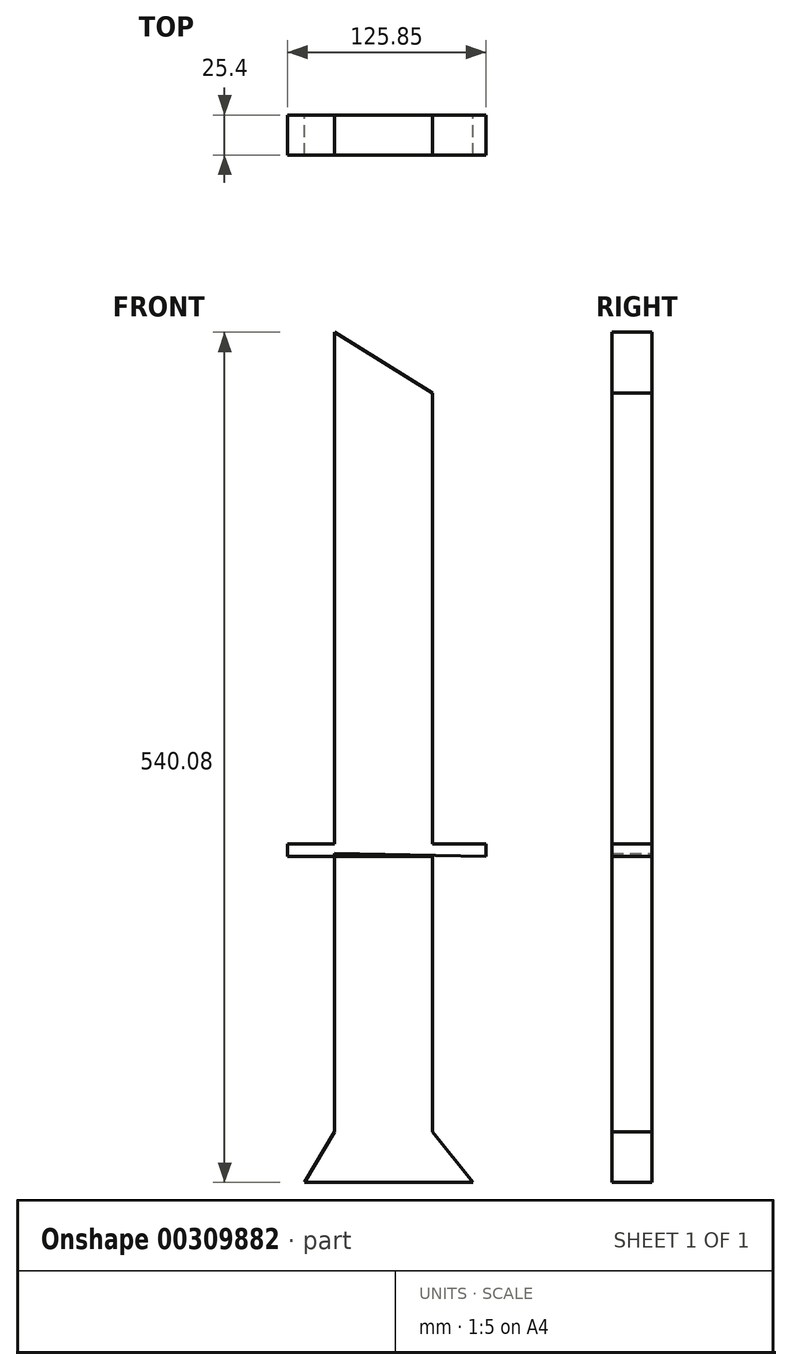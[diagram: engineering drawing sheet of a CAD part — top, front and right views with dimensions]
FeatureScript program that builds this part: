
annotation { "Feature Type Name" : "Feature", "Feature Type Description" : "" }
export const myFeature = defineFeature(function(context is Context, id is Id, definition is map)
    precondition{}
    {
        {
            var Q0;
            Q0=qCreatedBy(makeId("Front.planeOp"),FACE);
            var sketch = newSketch(context, id + "F0", { "sketchPlane" : qUnion([Q0])});
            skLineSegment(sketch, "E0.bottom", {"start": v(-29.82, 5.84) * mm, "end": v(78.28, 5.84) * mm});
            skLineSegment(sketch, "E0.top", {"start": v(-29.82, -2.03) * mm, "end": v(78.28, -2.03) * mm});
            skLineSegment(sketch, "E0.left", {"start": v(-29.82, 5.84) * mm, "end": v(-29.82, -2.03) * mm});
            skLineSegment(sketch, "E0.right", {"start": v(78.28, 5.84) * mm, "end": v(78.28, -2.03) * mm});
            skLineSegment(sketch, "E1", {"start": v(0, 5.84) * mm, "end": v(0, 331) * mm});
            skLineSegment(sketch, "E2", {"start": v(0, 331) * mm, "end": v(62.25, 292.4) * mm});
            skLineSegment(sketch, "E3", {"start": v(62.25, 292.4) * mm, "end": v(62.25, -2.03) * mm});
            skLineSegment(sketch, "E4", {"start": v(62.25, -2.03) * mm, "end": v(62.25, -176.94) * mm});
            skLineSegment(sketch, "E5", {"start": v(62.25, -176.94) * mm, "end": v(0, -176.94) * mm});
            skLineSegment(sketch, "E6", {"start": v(0, -176.94) * mm, "end": v(0, 0) * mm});
            skLineSegment(sketch, "E7", {"start": v(0, 0) * mm, "end": v(96.03, -2.03) * mm});
            skLineSegment(sketch, "E8", {"start": v(96.03, -2.03) * mm, "end": v(96.03, 5.84) * mm});
            skLineSegment(sketch, "E9", {"start": v(96.03, 5.84) * mm, "end": v(62.25, 5.84) * mm});
            skLineSegment(sketch, "E10", {"start": v(0, -176.94) * mm, "end": v(-19, -209.08) * mm});
            skLineSegment(sketch, "E11", {"start": v(-19, -209.08) * mm, "end": v(87.79, -209.08) * mm});
            skLineSegment(sketch, "E12", {"start": v(87.79, -209.08) * mm, "end": v(62.25, -176.94) * mm});
            skSolve(sketch);
        }
        {
            var Q0;
            {var subQ0=sQuery(id+"F0.wireOp",EDGE,"E4");Q0=makeQuery(id+"F0.imprint","IMPRINT",FACE,{"disambiguationData":[TD([[makeQuery(id+"F0.imprint","IMPRINT",EDGE,{"derivedFrom":subQ0}),-1.0]])]});}
            var Q1;
            {var subQ3=sQuery(id+"F0.wireOp",EDGE,"E1");Q1=makeQuery(id+"F0.imprint","IMPRINT",FACE,{"disambiguationData":[TD([[makeQuery(id+"F0.imprint","IMPRINT",EDGE,{"derivedFrom":subQ3}),-1.0]])]});}
            var Q2;
            {var subQ0=sQuery(id+"F0.wireOp",EDGE,"E9");var subQ1=sQuery(id+"F0.wireOp",EDGE,"E0.right");var subQ2=makeQuery(id+"F0.imprint","INTERSECT",VERTEX,{"derivedFrom":[subQ1,subQ0]});Q2=makeQuery(id+"F0.imprint","IMPRINT",FACE,{"disambiguationData":[TD([[makeQuery(id+"F0.imprint","IMPRINT",EDGE,{"disambiguationData":[TD([[subQ2,-1.0]])],"derivedFrom":subQ1}),-1.0]])]});}
            var Q3;
            {var subQ5=sQuery(id+"F0.wireOp",EDGE,"E8");Q3=makeQuery(id+"F0.imprint","IMPRINT",FACE,{"disambiguationData":[TD([[makeQuery(id+"F0.imprint","IMPRINT",EDGE,{"derivedFrom":subQ5}),1.0]])]});}
            var Q4;
            {var subQ0=sQuery(id+"F0.wireOp",EDGE,"E0.left");Q4=makeQuery(id+"F0.imprint","IMPRINT",FACE,{"disambiguationData":[TD([[makeQuery(id+"F0.imprint","IMPRINT",EDGE,{"derivedFrom":subQ0}),1.0]])]});}
            extrude(context, id + "F1", {"entities" : qUnion([Q0, Q1, Q2, Q3, Q4]), "endBound" : BoundingType.SYMMETRIC, "depth" : 25.4 * mm});
        }
        {
            var Q0;
            Q0=makeQuery(id+"F0.imprint","IMPRINT",FACE,{"disambiguationData":[TD([[makeQuery(id+"F0.imprint","IMPRINT",EDGE,{"derivedFrom":sQuery(id+"F0.wireOp",EDGE,"E5")}),1.0]])]});
            extrude(context, id + "F2", {"entities" : qUnion([Q0]), "operationType" : NewBodyOperationType.ADD, "endBound" : BoundingType.SYMMETRIC, "depth" : 25.4 * mm});
        }
    });
